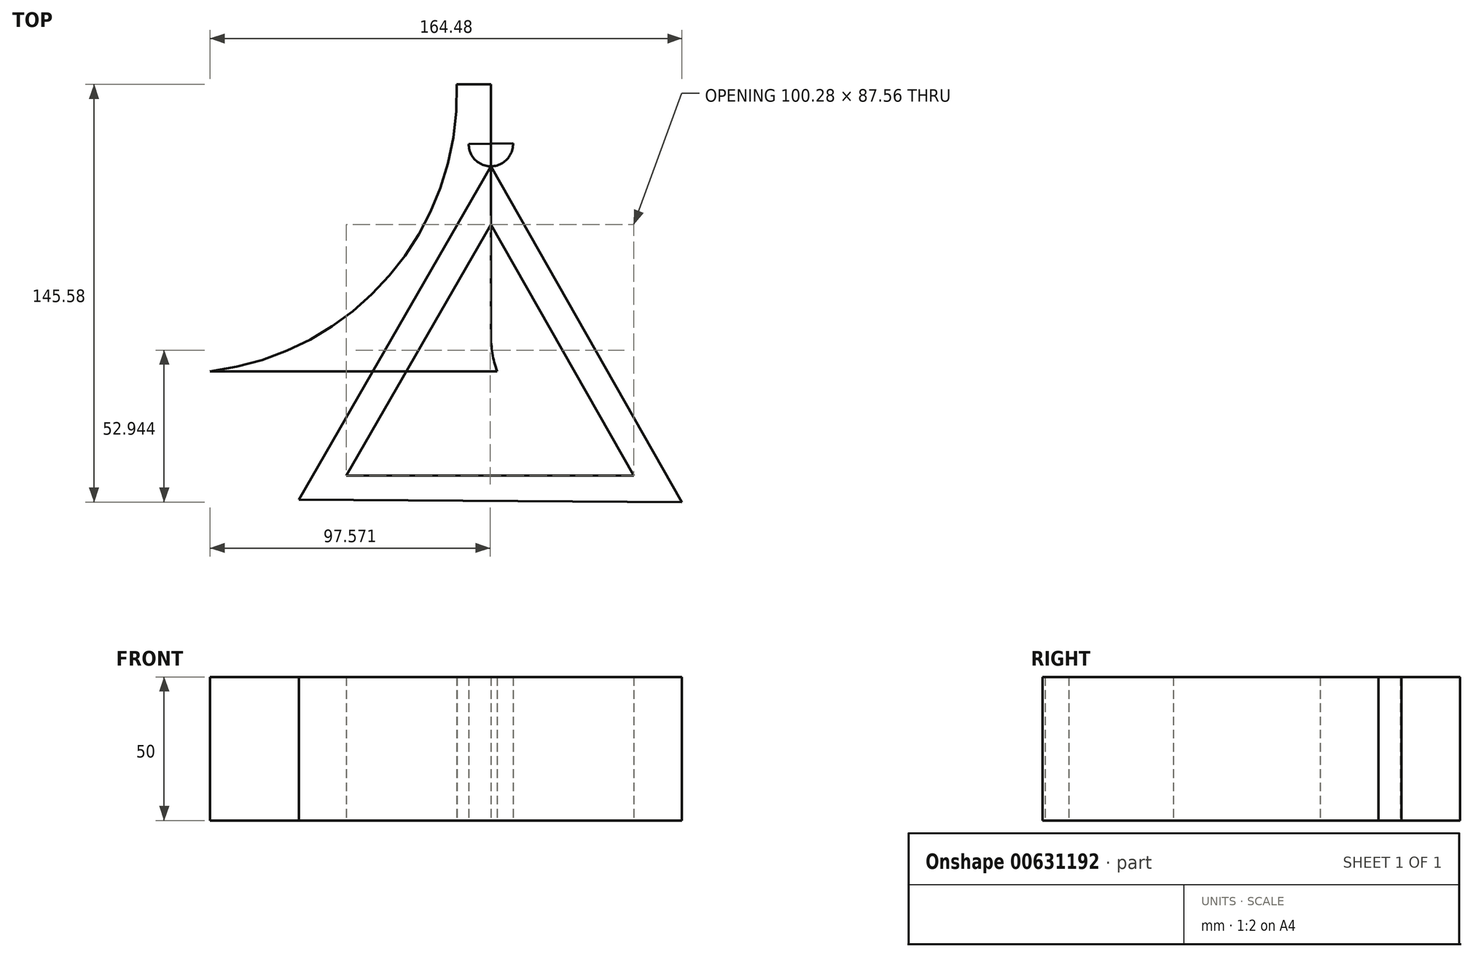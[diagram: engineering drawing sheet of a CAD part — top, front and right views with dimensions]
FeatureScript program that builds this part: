
annotation { "Feature Type Name" : "Feature", "Feature Type Description" : "" }
export const myFeature = defineFeature(function(context is Context, id is Id, definition is map)
    precondition{}
    {
        {
            var Q0;
            Q0=qCreatedBy(makeId("Top.planeOp"),FACE);
            var sketch = newSketch(context, id + "F0", { "sketchPlane" : qUnion([Q0])});
            skLineSegment(sketch, "E0", {"start": v(0, 87.3) * mm, "end": v(0, 0) * mm});
            skArc(sketch, "E1", {"start": v(0, 0) * mm, "mid": v(0.54, -6.44) * mm, "end": v(2.14, -12.7) * mm});
            skLineSegment(sketch, "E2", {"start": v(2.14, -12.7) * mm, "end": v(-97.86, -12.7) * mm});
            skLineSegment(sketch, "E3", {"start": v(0, 87.3) * mm, "end": v(-11.9, 87.3) * mm});
            skArc(sketch, "E4", {"start": v(-97.86, -12.7) * mm, "mid": v(-35.45, 20.59) * mm, "end": v(-11.9, 87.3) * mm});
            skSolve(sketch);
        }
        {
            var Q0;
            Q0=makeQuery(id+"F0.imprint","IMPRINT",FACE,{"disambiguationData":[TD([[makeQuery(id+"F0.imprint","IMPRINT",EDGE,{"derivedFrom":sQuery(id+"F0.wireOp",EDGE,"E0")}),-1.0]])]});
            extrude(context, id + "F1", {"entities" : qUnion([Q0]), "depth" : 50 * mm, "offsetDistance" : 25 * mm});
        }
        {
            var Q0;
            Q0=qCreatedBy(makeId("Top.planeOp"),FACE);
            var sketch = newSketch(context, id + "F2", { "sketchPlane" : qUnion([Q0])});
            skLineSegment(sketch, "E5", {"start": v(-50.43, -49.13) * mm, "end": v(49.85, -49.13) * mm});
            skLineSegment(sketch, "E6", {"start": v(49.85, -49.13) * mm, "end": v(0, 38.44) * mm});
            skLineSegment(sketch, "E7", {"start": v(0, 38.44) * mm, "end": v(-50.43, -49.13) * mm});
            skLineSegment(sketch, "E8", {"start": v(61.41, -49.13) * mm, "end": v(0, 58.74) * mm});
            skLineSegment(sketch, "E9", {"start": v(0, 58.74) * mm, "end": v(-66.92, -57.46) * mm});
            skLineSegment(sketch, "E10", {"start": v(61.41, -49.13) * mm, "end": v(66.62, -58.29) * mm});
            skLineSegment(sketch, "E11", {"start": v(66.62, -58.29) * mm, "end": v(-66.92, -57.46) * mm});
            skLineSegment(sketch, "E12", {"start": v(-7.73, 66.47) * mm, "end": v(-7.73, 66.47) * mm});
            skArc(sketch, "E13", {"start": v(-7.73, 66.47) * mm, "mid": v(0.14, 58.74) * mm, "end": v(7.72, 66.75) * mm});
            skPoint(sketch, "E14.end.orphan", {"position": v(7.72, 66.83) * mm});
            skPoint(sketch, "E15.orphan", {"position": v(11.76, 66.83) * mm});
            skLineSegment(sketch, "E16", {"start": v(-7.73, 66.47) * mm, "end": v(7.72, 66.75) * mm});
            skSolve(sketch);
        }
        {
            var Q0;
            Q0 = qSketchRegion(id + "F2", true);
            extrude(context, id + "F3", {"entities" : qUnion([Q0]), "depth" : 50 * mm, "offsetDistance" : 25 * mm});
        }
    });
